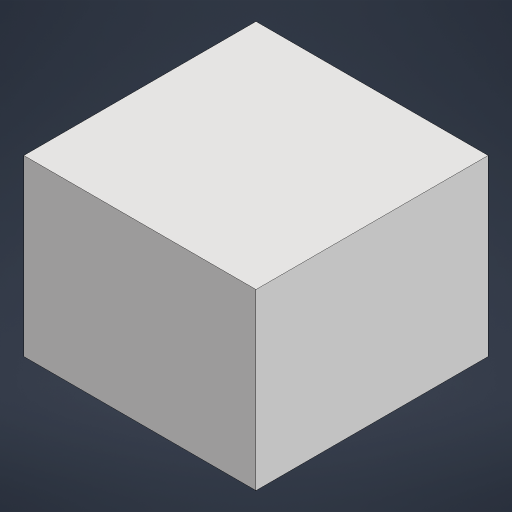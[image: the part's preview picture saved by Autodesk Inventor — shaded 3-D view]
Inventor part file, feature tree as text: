
AUTODESK INVENTOR PART (.ipt)
format: ipt  version: 2023.1 (Build 271208000, 208)  size: 122,880 bytes
history: native  units: in
note: dims shown in document units (in); Inventor stores cm internally (conversion verified against a paired STEP export)
features: extrude x1, sketch x1
ambient origin geometry x8: Origin, YZ Plane, XZ Plane, XY Plane, X Axis, Y Axis, Z Axis, Center Point
bodies: Solid1 (feature_tree)
feature tree (2):
  extrude  "Extrusion1"  Depth=4.0in
  sketch  "Sketch2"  dims[d3=4.0in d4=4.0in d5=3.0in d6=0.0in]
